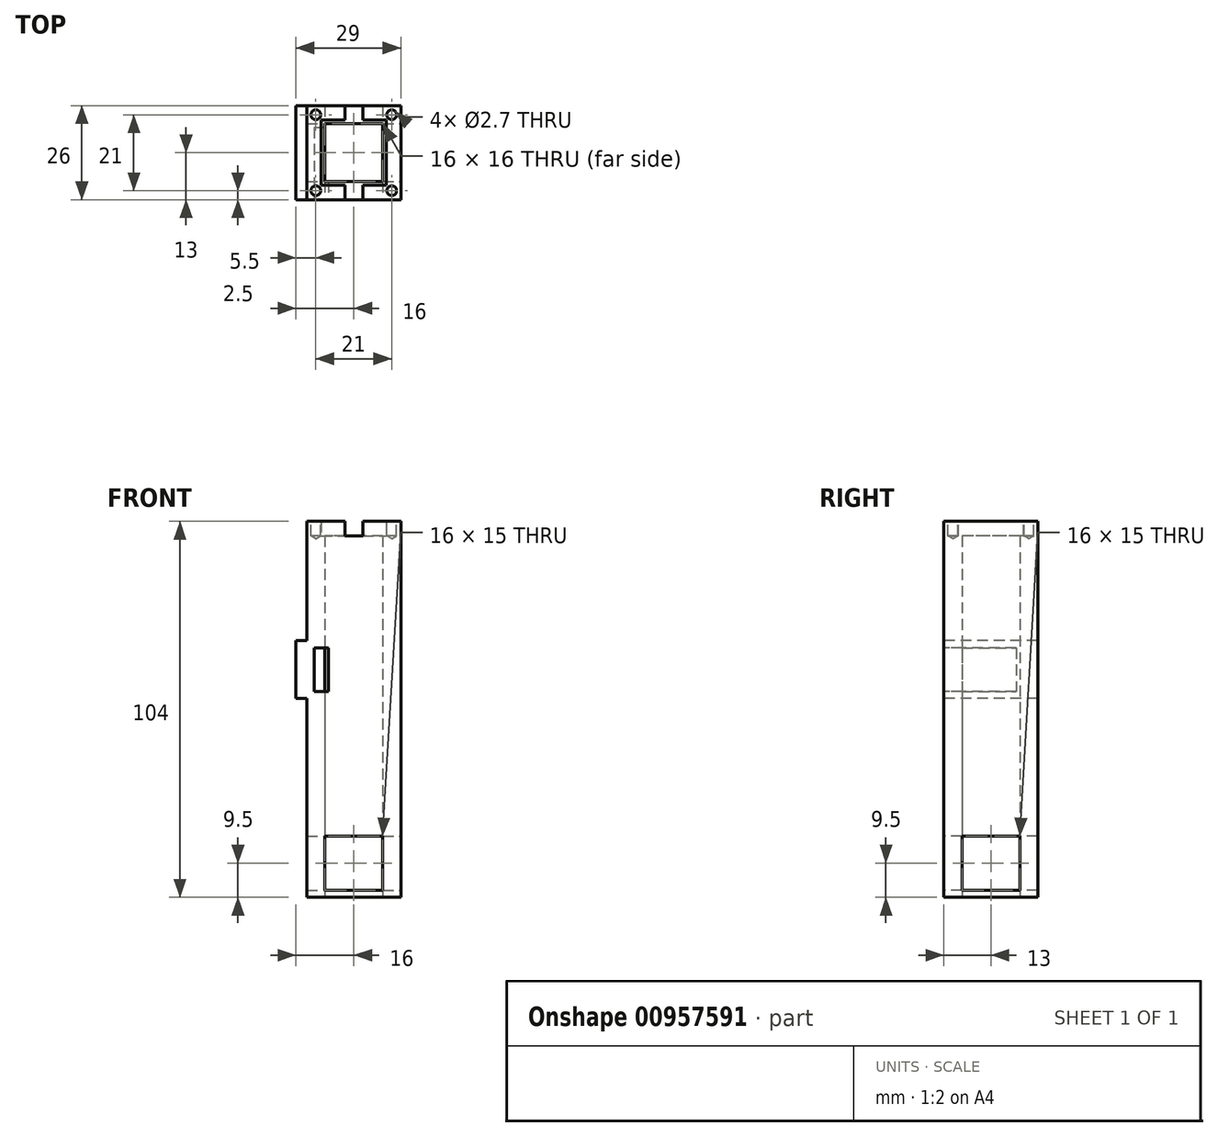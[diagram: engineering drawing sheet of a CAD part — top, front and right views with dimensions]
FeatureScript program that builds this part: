
annotation { "Feature Type Name" : "Feature", "Feature Type Description" : "" }
export const myFeature = defineFeature(function(context is Context, id is Id, definition is map)
    precondition{}
    {
        {
            var Q0;
            Q0=qCreatedBy(makeId("Top.planeOp"),FACE);
            var sketch = newSketch(context, id + "F0", { "sketchPlane" : qUnion([Q0])});
            skLineSegment(sketch, "E0.bottom", {"start": v(13, 13) * mm, "end": v(-13, 13) * mm});
            skLineSegment(sketch, "E0.top", {"start": v(13, -13) * mm, "end": v(-13, -13) * mm});
            skLineSegment(sketch, "E0.left", {"start": v(13, 13) * mm, "end": v(13, -13) * mm});
            skLineSegment(sketch, "E0.right", {"start": v(-13, 13) * mm, "end": v(-13, -13) * mm});
            skPoint(sketch, "E0.middle", {"position": v(0, 0) * mm});
            skLineSegment(sketch, "E1.bottom", {"start": v(8, 8) * mm, "end": v(-8, 8) * mm});
            skLineSegment(sketch, "E1.top", {"start": v(8, -8) * mm, "end": v(-8, -8) * mm});
            skLineSegment(sketch, "E1.left", {"start": v(8, 8) * mm, "end": v(8, -8) * mm});
            skLineSegment(sketch, "E1.right", {"start": v(-8, 8) * mm, "end": v(-8, -8) * mm});
            skSolve(sketch);
        }
        {
            var Q0;
            Q0=makeQuery(id+"F0.imprint","IMPRINT",FACE,{"disambiguationData":[TD([[makeQuery(id+"F0.imprint","IMPRINT",EDGE,{"derivedFrom":sQuery(id+"F0.wireOp",EDGE,"E0.bottom")}),1.0]])]});
            var Q1;
            Q1=makeQuery(id+"F0.imprint","IMPRINT",FACE,{"disambiguationData":[TD([[makeQuery(id+"F0.imprint","IMPRINT",EDGE,{"derivedFrom":sQuery(id+"F0.wireOp",EDGE,"E1.bottom")}),-1.0]])]});
            var Q2;
            Q2=makeQuery(id+"F0.imprint","IMPRINT",FACE,{"disambiguationData":[TD([[makeQuery(id+"F0.imprint","IMPRINT",EDGE,{"derivedFrom":sQuery(id+"F0.wireOp",EDGE,"E1.bottom")}),1.0]])]});
            extrude(context, id + "F1", {"entities" : qUnion([Q0, Q1, Q2]), "depth" : 2 * mm, "offsetDistance" : 25 * mm});
        }
        {
            var Q0;
            Q0=qSketchRegion(id+"F0",true);
            var Q1;
            Q1=makeQuery(id+"F0.imprint","IMPRINT",FACE,{"disambiguationData":[TD([[makeQuery(id+"F0.imprint","IMPRINT",EDGE,{"derivedFrom":sQuery(id+"F0.wireOp",EDGE,"E1.bottom")}),-1.0]])]});
            extrude(context, id + "F2", {"entities" : qUnion([Q0, Q1]), "operationType" : NewBodyOperationType.ADD, "depth" : 100 * mm, "offsetDistance" : 25 * mm});
        }
        {
            var Q0;
            Q0=makeQuery(id+"F2.opExtrude","CAP_FACE",FACE,{"disambiguationData":[OSD([sQuery(id+"F0.wireOp",EDGE,"E0.bottom"),sQuery(id+"F0.wireOp",EDGE,"E0.top"),sQuery(id+"F0.wireOp",EDGE,"E0.left"),sQuery(id+"F0.wireOp",EDGE,"E0.right"),sQuery(id+"F0.wireOp",EDGE,"E1.bottom"),sQuery(id+"F0.wireOp",EDGE,"E1.top"),sQuery(id+"F0.wireOp",EDGE,"E1.left"),sQuery(id+"F0.wireOp",EDGE,"E1.right")])],"isStart":false});
            var sketch = newSketch(context, id + "F3", { "sketchPlane" : qUnion([Q0])});
            skLineSegment(sketch, "E2.bottom", {"start": v(-9, 9) * mm, "end": v(9, 9) * mm});
            skLineSegment(sketch, "E2.top", {"start": v(-9, -9) * mm, "end": v(9, -9) * mm});
            skLineSegment(sketch, "E2.left", {"start": v(-9, 9) * mm, "end": v(-9, -9) * mm});
            skLineSegment(sketch, "E2.right", {"start": v(9, 9) * mm, "end": v(9, -9) * mm});
            skPoint(sketch, "E2.middle", {"position": v(0, 0) * mm});
            skSolve(sketch);
        }
        {
            var Q0;
            Q0=makeQuery(id+"F3.imprint","IMPRINT",FACE,{"disambiguationData":[TD([[makeQuery(id+"F3.imprint","IMPRINT",EDGE,{"derivedFrom":sQuery(id+"F3.wireOp",EDGE,"E2.bottom")}),1.0]])]});
            extrude(context, id + "F4", {"entities" : qUnion([Q0]), "operationType" : NewBodyOperationType.ADD, "depth" : 4 * mm, "offsetDistance" : 25 * mm});
        }
        {
            var Q0;
            Q0=makeQuery(id+"F4.opExtrude","CAP_FACE",FACE,{"disambiguationData":[OSD([sQuery(id+"F0.wireOp",EDGE,"E0.bottom"),sQuery(id+"F0.wireOp",EDGE,"E0.top"),sQuery(id+"F0.wireOp",EDGE,"E0.left"),sQuery(id+"F0.wireOp",EDGE,"E0.right"),sQuery(id+"F3.wireOp",EDGE,"E2.bottom"),sQuery(id+"F3.wireOp",EDGE,"E2.top"),sQuery(id+"F3.wireOp",EDGE,"E2.left"),sQuery(id+"F3.wireOp",EDGE,"E2.right")])],"isStart":false});
            var sketch = newSketch(context, id + "F5", { "sketchPlane" : qUnion([Q0])});
            skLineSegment(sketch, "E3", {"start": v(-2.5, 13) * mm, "end": v(-2.5, 9) * mm});
            skLineSegment(sketch, "E4.MirrorCS", {"start": v(2.5, 13) * mm, "end": v(2.5, 9) * mm});
            skLineSegment(sketch, "E5.MirrorCS", {"start": v(2.5, -13) * mm, "end": v(2.5, -9) * mm});
            skLineSegment(sketch, "E6.MirrorCS", {"start": v(-2.5, -13) * mm, "end": v(-2.5, -9) * mm});
            skLineSegment(sketch, "E7", {"start": v(-13, 13) * mm, "end": v(-9, 9) * mm, "construction": true});
            skPoint(sketch, "E8", {"position": v(-10.5, 10.5) * mm});
            skPoint(sketch, "E9.MirrorP", {"position": v(10.5, 10.5) * mm});
            skLineSegment(sketch, "E10.MirrorCS", {"start": v(13, 13) * mm, "end": v(9, 9) * mm, "construction": true});
            skLineSegment(sketch, "E11.MirrorCS", {"start": v(-13, -13) * mm, "end": v(-9, -9) * mm, "construction": true});
            skPoint(sketch, "E12.MirrorP", {"position": v(-10.5, -10.5) * mm});
            skLineSegment(sketch, "E13.MirrorCS", {"start": v(13, -13) * mm, "end": v(9, -9) * mm, "construction": true});
            skPoint(sketch, "E14.MirrorP", {"position": v(10.5, -10.5) * mm});
            skSolve(sketch);
        }
        {
            var Q0;
            {var subQ0=sQuery(id+"F5.wireOp",EDGE,"E5.MirrorCS");Q0=makeQuery(id+"F5.imprint","IMPRINT",FACE,{"disambiguationData":[TD([[makeQuery(id+"F5.imprint","IMPRINT",EDGE,{"derivedFrom":subQ0}),1.0]])]});}
            var Q1;
            {var subQ0=sQuery(id+"F5.wireOp",EDGE,"E3");Q1=makeQuery(id+"F5.imprint","IMPRINT",FACE,{"disambiguationData":[TD([[makeQuery(id+"F5.imprint","IMPRINT",EDGE,{"derivedFrom":subQ0}),1.0]])]});}
            var Q2;
            Q2=makeQuery(id+"F2.opExtrude","CAP_FACE",FACE,{"disambiguationData":[OSD([sQuery(id+"F0.wireOp",EDGE,"E0.bottom"),sQuery(id+"F0.wireOp",EDGE,"E0.top"),sQuery(id+"F0.wireOp",EDGE,"E0.left"),sQuery(id+"F0.wireOp",EDGE,"E0.right"),sQuery(id+"F0.wireOp",EDGE,"E1.bottom"),sQuery(id+"F0.wireOp",EDGE,"E1.top"),sQuery(id+"F0.wireOp",EDGE,"E1.left"),sQuery(id+"F0.wireOp",EDGE,"E1.right")])],"isStart":false});
            extrude(context, id + "F6", {"entities" : qUnion([Q0, Q1]), "operationType" : NewBodyOperationType.REMOVE, "endBound" : BoundingType.UP_TO_SURFACE, "oppositeDirection" : true, "depth" : 25 * mm, "endBoundEntityFace" : qUnion([Q2]), "offsetDistance" : 25 * mm});
        }
        {
            var Q0;
            Q0=sQuery(id+"F5.wireOp",VERTEX,"E8");
            var Q1;
            Q1=sQuery(id+"F5.wireOp",VERTEX,"E9.MirrorP");
            var Q2;
            Q2=sQuery(id+"F5.wireOp",VERTEX,"E12.MirrorP");
            var Q3;
            Q3=sQuery(id+"F5.wireOp",VERTEX,"E14.MirrorP");
            var Q4;
            Q4=makeQuery(id+"F1.opExtrude","SWEPT_BODY",BODY,{"disambiguationData":[OSD([sQuery(id+"F0.wireOp",EDGE,"E0.bottom"),sQuery(id+"F0.wireOp",EDGE,"E0.top"),sQuery(id+"F0.wireOp",EDGE,"E0.left"),sQuery(id+"F0.wireOp",EDGE,"E0.right")])]});
            hole(context, id + "F7", {"style" : HoleStyle.SIMPLE, "endStyle" : HoleEndStyle.BLIND, "standardTappedOrClearance" : lookupTablePath({ "standard" : "ISO", "engagement" : "50%", "pitch" : "0.5 mm", "size" : "M3", "type" : "Tapped" }), "standardBlindInLast" : lookupTablePath({ "standard" : "ISO", "fit" : "Normal", "engagement" : "50%", "pitch" : "0.5 mm", "size" : "M3", "type" : "Clearance & tapped" }), "holeDiameter" : 2.7 * mm, "majorDiameter" : 3 * mm, "showTappedDepth" : true, "holeDepth" : 4 * mm, "isTappedThrough" : true, "tappedDepth" : 2.5 * mm, "tapClearance" : 3, "locations" : qUnion([Q0, Q1, Q2, Q3]), "scope" : qUnion([Q4])});
        }
        {
            var Q0;
            {var subQ0=sQuery(id+"F0.wireOp",EDGE,"E0.left");Q0=makeQuery(id+"F4.boolean.opBoolean","MERGE",FACE,{"derivedFrom":[makeQuery(id+"F2.boolean.opBoolean","MERGE",FACE,{"derivedFrom":[makeQuery(id+"F1.opExtrude","SWEPT_FACE",FACE,{"disambiguationData":[OSD([subQ0])]}),makeQuery(id+"F2.opExtrude","SWEPT_FACE",FACE,{"disambiguationData":[OSD([subQ0])]})]}),makeQuery(id+"F4.opExtrude","SWEPT_FACE",FACE,{"disambiguationData":[OSD([subQ0])]})]});}
            var sketch = newSketch(context, id + "F8", { "sketchPlane" : qUnion([Q0])});
            skLineSegment(sketch, "E15.bottom", {"start": v(-7.98, 98) * mm, "end": v(8.02, 98) * mm});
            skLineSegment(sketch, "E15.top", {"start": v(-7.98, 2) * mm, "end": v(8.02, 2) * mm});
            skLineSegment(sketch, "E15.left", {"start": v(-7.98, 98) * mm, "end": v(-7.98, 2) * mm});
            skLineSegment(sketch, "E15.right", {"start": v(8.02, 98) * mm, "end": v(8.02, 2) * mm});
            skLineSegment(sketch, "E16", {"start": v(-7.98, 0) * mm, "end": v(-7.98, 100) * mm, "construction": true});
            skLineSegment(sketch, "E17", {"start": v(8.02, 0) * mm, "end": v(8.02, 100) * mm, "construction": true});
            skSolve(sketch);
        }
        {
            var Q0;
            Q0=makeQuery(id+"F0.imprint","IMPRINT",FACE,{"disambiguationData":[TD([[makeQuery(id+"F0.imprint","IMPRINT",EDGE,{"derivedFrom":sQuery(id+"F0.wireOp",EDGE,"E1.bottom")}),1.0]])]});
            extrude(context, id + "F9", {"entities" : qUnion([Q0]), "operationType" : NewBodyOperationType.REMOVE, "depth" : 25 * mm, "offsetDistance" : 25 * mm});
        }
        {
            var Q0;
            {var subQ0=sQuery(id+"F0.wireOp",EDGE,"E0.top");Q0=makeQuery(id+"F4.boolean.opBoolean","MERGE",FACE,{"derivedFrom":[makeQuery(id+"F2.boolean.opBoolean","MERGE",FACE,{"derivedFrom":[makeQuery(id+"F1.opExtrude","SWEPT_FACE",FACE,{"disambiguationData":[OSD([subQ0])]}),makeQuery(id+"F2.opExtrude","SWEPT_FACE",FACE,{"disambiguationData":[OSD([subQ0])]})]}),makeQuery(id+"F4.opExtrude","SWEPT_FACE",FACE,{"disambiguationData":[OSD([subQ0])]})]});}
            var sketch = newSketch(context, id + "F10", { "sketchPlane" : qUnion([Q0])});
            skLineSegment(sketch, "E18.bottom", {"start": v(-13, 55) * mm, "end": v(-16, 55) * mm});
            skLineSegment(sketch, "E18.top", {"start": v(-13, 71) * mm, "end": v(-16, 71) * mm});
            skLineSegment(sketch, "E18.left", {"start": v(-13, 71) * mm, "end": v(-13, 55) * mm});
            skLineSegment(sketch, "E18.right", {"start": v(-16, 71) * mm, "end": v(-16, 55) * mm});
            skSolve(sketch);
        }
        {
            var Q0;
            Q0 = qSketchRegion(id + "F10", true);
            extrude(context, id + "F11", {"entities" : qUnion([Q0]), "operationType" : NewBodyOperationType.ADD, "oppositeDirection" : true, "depth" : 26 * mm, "offsetDistance" : 25 * mm});
        }
        {
            var Q0;
            {var subQ0=sQuery(id+"F0.wireOp",EDGE,"E0.top");Q0=makeQuery(id+"F11.boolean.opBoolean","MERGE",FACE,{"derivedFrom":[makeQuery(id+"F4.boolean.opBoolean","MERGE",FACE,{"derivedFrom":[makeQuery(id+"F2.boolean.opBoolean","MERGE",FACE,{"derivedFrom":[makeQuery(id+"F1.opExtrude","SWEPT_FACE",FACE,{"disambiguationData":[OSD([subQ0])]}),makeQuery(id+"F2.opExtrude","SWEPT_FACE",FACE,{"disambiguationData":[OSD([subQ0])]})]}),makeQuery(id+"F4.opExtrude","SWEPT_FACE",FACE,{"disambiguationData":[OSD([subQ0])]})]}),makeQuery(id+"F11.opExtrude","CAP_FACE",FACE,{"disambiguationData":[OSD([sQuery(id+"F10.wireOp",EDGE,"E18.bottom"),sQuery(id+"F10.wireOp",EDGE,"E18.top"),sQuery(id+"F10.wireOp",EDGE,"E18.left"),sQuery(id+"F10.wireOp",EDGE,"E18.right")])],"isStart":true})]});}
            var sketch = newSketch(context, id + "F12", { "sketchPlane" : qUnion([Q0])});
            skLineSegment(sketch, "E19.bottom", {"start": v(-11, 69) * mm, "end": v(-7, 69) * mm});
            skLineSegment(sketch, "E19.top", {"start": v(-11, 57) * mm, "end": v(-7, 57) * mm});
            skLineSegment(sketch, "E19.left", {"start": v(-11, 69) * mm, "end": v(-11, 57) * mm});
            skLineSegment(sketch, "E19.right", {"start": v(-7, 69) * mm, "end": v(-7, 57) * mm});
            skSolve(sketch);
        }
        {
            var Q0;
            Q0 = qSketchRegion(id + "F12", true);
            extrude(context, id + "F13", {"entities" : qUnion([Q0]), "operationType" : NewBodyOperationType.REMOVE, "oppositeDirection" : true, "depth" : 20 * mm, "offsetDistance" : 25 * mm});
        }
        {
            var Q0;
            {var subQ0=sQuery(id+"F0.wireOp",EDGE,"E0.top");Q0=makeQuery(id+"F11.boolean.opBoolean","MERGE",FACE,{"derivedFrom":[makeQuery(id+"F4.boolean.opBoolean","MERGE",FACE,{"derivedFrom":[makeQuery(id+"F2.boolean.opBoolean","MERGE",FACE,{"derivedFrom":[makeQuery(id+"F1.opExtrude","SWEPT_FACE",FACE,{"disambiguationData":[OSD([subQ0])]}),makeQuery(id+"F2.opExtrude","SWEPT_FACE",FACE,{"disambiguationData":[OSD([subQ0])]})]}),makeQuery(id+"F4.opExtrude","SWEPT_FACE",FACE,{"disambiguationData":[OSD([subQ0])]})]}),makeQuery(id+"F11.opExtrude","CAP_FACE",FACE,{"disambiguationData":[OSD([sQuery(id+"F10.wireOp",EDGE,"E18.bottom"),sQuery(id+"F10.wireOp",EDGE,"E18.top"),sQuery(id+"F10.wireOp",EDGE,"E18.left"),sQuery(id+"F10.wireOp",EDGE,"E18.right")])],"isStart":true})]});}
            var sketch = newSketch(context, id + "F14", { "sketchPlane" : qUnion([Q0])});
            skLineSegment(sketch, "E20.bottom", {"start": v(-8, 2) * mm, "end": v(8, 2) * mm});
            skLineSegment(sketch, "E20.top", {"start": v(-8, 17) * mm, "end": v(8, 17) * mm});
            skLineSegment(sketch, "E20.left", {"start": v(-8, 2) * mm, "end": v(-8, 17) * mm});
            skLineSegment(sketch, "E20.right", {"start": v(8, 2) * mm, "end": v(8, 17) * mm});
            skSolve(sketch);
        }
        {
            var Q0;
            Q0 = qSketchRegion(id + "F14", true);
            extrude(context, id + "F15", {"entities" : qUnion([Q0]), "operationType" : NewBodyOperationType.REMOVE, "oppositeDirection" : true, "depth" : 40 * mm, "offsetDistance" : 25 * mm});
        }
        {
            var Q0;
            Q0=makeQuery(id+"F8.imprint","IMPRINT",FACE,{"disambiguationData":[TD([[makeQuery(id+"F8.imprint","IMPRINT",EDGE,{"derivedFrom":sQuery(id+"F8.wireOp",EDGE,"E15.bottom")}),-1.0]])]});
            var sketch = newSketch(context, id + "F16", { "sketchPlane" : qUnion([Q0])});
            skLineSegment(sketch, "E21.bottom", {"start": v(-8, 2) * mm, "end": v(8, 2) * mm});
            skLineSegment(sketch, "E21.top", {"start": v(-8, 17) * mm, "end": v(8, 17) * mm});
            skLineSegment(sketch, "E21.left", {"start": v(-8, 2) * mm, "end": v(-8, 17) * mm});
            skLineSegment(sketch, "E21.right", {"start": v(8, 2) * mm, "end": v(8, 17) * mm});
            skSolve(sketch);
        }
        {
            var Q0;
            Q0 = qSketchRegion(id + "F16", true);
            extrude(context, id + "F17", {"entities" : qUnion([Q0]), "operationType" : NewBodyOperationType.REMOVE, "oppositeDirection" : true, "depth" : 40 * mm, "offsetDistance" : 25 * mm});
        }
    });
